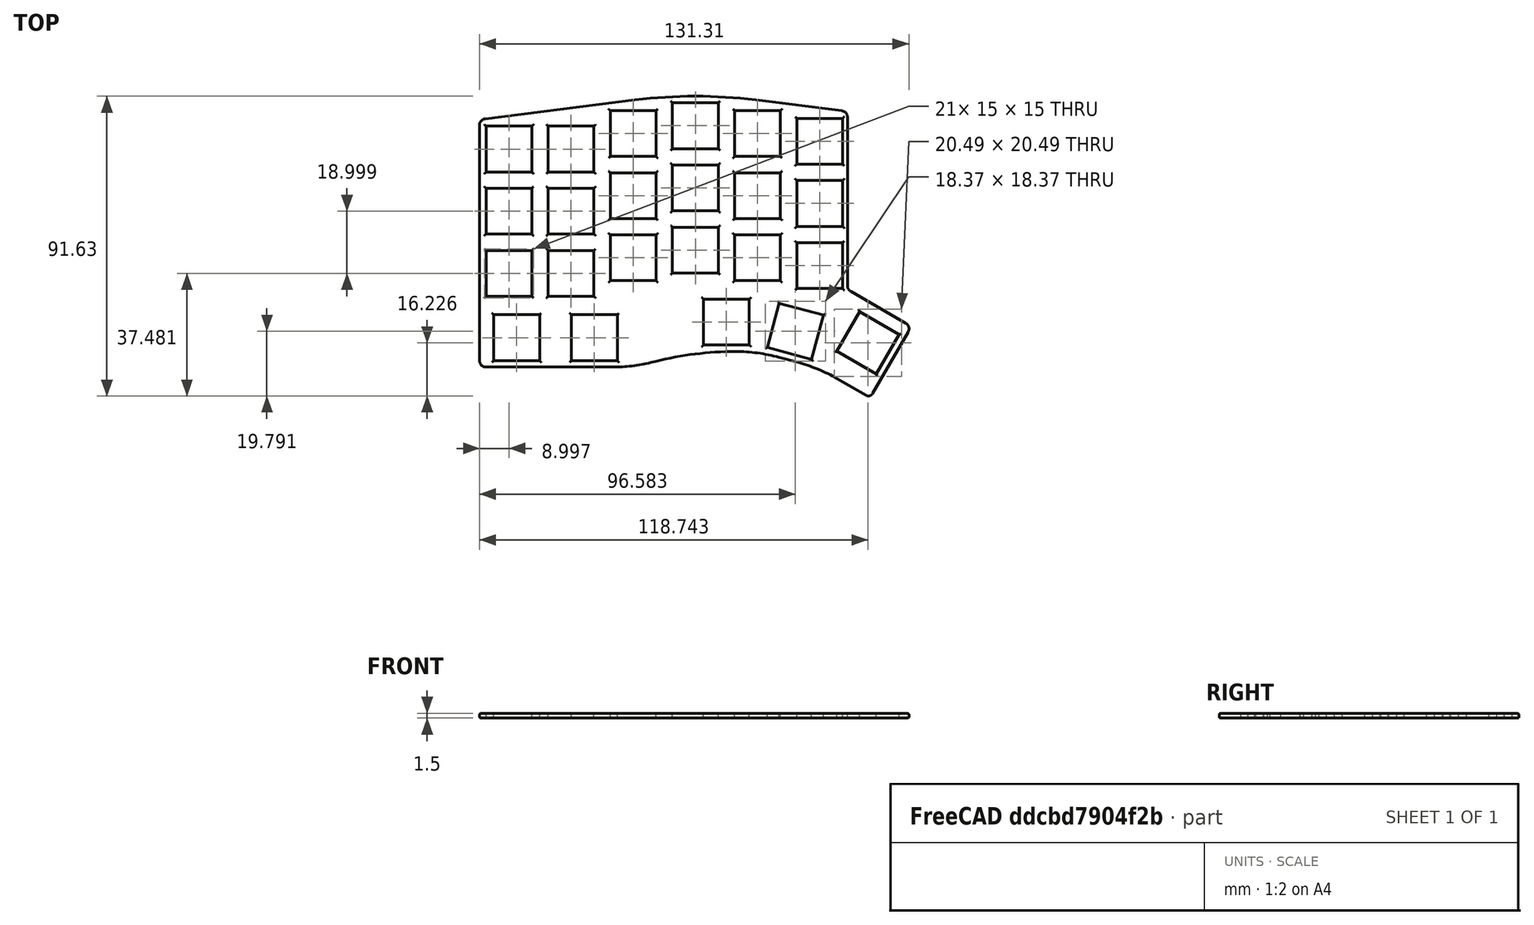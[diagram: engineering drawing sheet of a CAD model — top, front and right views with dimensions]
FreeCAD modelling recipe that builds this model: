
FCSTD DOCUMENT  (FreeCAD 0.21R)
Label: plate
License: All rights reserved
LicenseURL: http://en.wikipedia.org/wiki/All_rights_reserved
objects: Sketcher::SketchObject×1, PartDesign::Pad×1, PartDesign::Fillet×1, PartDesign::Body×1
note: 6 computed .brp shape members not serialized (recipe doc carries the construction recipe); baked Part::Feature solids carry a one-line shape summary decoded from their .brp

FEATURE [Sketcher::SketchObject] Sketch
  FullyConstrained = false
  sketch-geometry (113):
    g0: LineSegment StartX=-4.87291 StartY=42.5634 StartZ=0 EndX=9.12709 EndY=42.5634 EndZ=0
    g1: LineSegment StartX=-4.87291 StartY=28.5634 StartZ=0 EndX=9.12709 EndY=28.5634 EndZ=0
    g2: LineSegment StartX=-4.87291 StartY=42.5634 StartZ=0 EndX=-4.87291 EndY=28.5634 EndZ=0
    g3: LineSegment StartX=9.12709 StartY=42.5634 StartZ=0 EndX=9.12709 EndY=28.5634 EndZ=0
    g4: LineSegment StartX=-23.8729 StartY=40.1885 StartZ=0 EndX=-9.87291 EndY=40.1885 EndZ=0
    g5: LineSegment StartX=-23.8729 StartY=26.1885 StartZ=0 EndX=-9.87291 EndY=26.1885 EndZ=0
    g6: LineSegment StartX=-23.8729 StartY=40.1885 StartZ=0 EndX=-23.8729 EndY=26.1885 EndZ=0
    g7: LineSegment StartX=-9.87291 StartY=40.1885 StartZ=0 EndX=-9.87291 EndY=26.1885 EndZ=0
    g8: LineSegment StartX=14.1271 StartY=40.1885 StartZ=0 EndX=28.1271 EndY=40.1885 EndZ=0
    g9: LineSegment StartX=14.1271 StartY=26.1885 StartZ=0 EndX=28.1271 EndY=26.1885 EndZ=0
    g10: LineSegment StartX=14.1271 StartY=40.1885 StartZ=0 EndX=14.1271 EndY=26.1885 EndZ=0
    g11: LineSegment StartX=28.1271 StartY=40.1885 StartZ=0 EndX=28.1271 EndY=26.1885 EndZ=0
    g12: LineSegment StartX=33.1271 StartY=37.8136 StartZ=0 EndX=47.1271 EndY=37.8136 EndZ=0
    g13: LineSegment StartX=33.1271 StartY=23.8136 StartZ=0 EndX=47.1271 EndY=23.8136 EndZ=0
    g14: LineSegment StartX=33.1271 StartY=37.8136 StartZ=0 EndX=33.1271 EndY=23.8136 EndZ=0
    g15: LineSegment StartX=47.1271 StartY=37.8136 StartZ=0 EndX=47.1271 EndY=23.8136 EndZ=0
    g16: LineSegment StartX=-61.8729 StartY=35.4388 StartZ=0 EndX=-47.8729 EndY=35.4388 EndZ=0
    g17: LineSegment StartX=-61.8729 StartY=21.4388 StartZ=0 EndX=-47.8729 EndY=21.4388 EndZ=0
    g18: LineSegment StartX=-61.8729 StartY=35.4388 StartZ=0 EndX=-61.8729 EndY=21.4388 EndZ=0
    g19: LineSegment StartX=-47.8729 StartY=35.4388 StartZ=0 EndX=-47.8729 EndY=21.4388 EndZ=0
    g20: LineSegment StartX=-42.8729 StartY=35.4388 StartZ=0 EndX=-28.8729 EndY=35.4388 EndZ=0
    g21: LineSegment StartX=-42.8729 StartY=21.4388 StartZ=0 EndX=-28.8729 EndY=21.4388 EndZ=0
    g22: LineSegment StartX=-42.8729 StartY=35.4388 StartZ=0 EndX=-42.8729 EndY=21.4388 EndZ=0
    g23: LineSegment StartX=-28.8729 StartY=35.4388 StartZ=0 EndX=-28.8729 EndY=21.4388 EndZ=0
    g24: LineSegment StartX=-4.87291 StartY=23.5644 StartZ=0 EndX=9.12709 EndY=23.5644 EndZ=0
    g25: LineSegment StartX=-4.87291 StartY=9.56439 StartZ=0 EndX=9.12709 EndY=9.56439 EndZ=0
    g26: LineSegment StartX=-4.87291 StartY=23.5644 StartZ=0 EndX=-4.87291 EndY=9.56439 EndZ=0
    g27: LineSegment StartX=9.12709 StartY=23.5644 StartZ=0 EndX=9.12709 EndY=9.56439 EndZ=0
    g28: LineSegment StartX=-23.8729 StartY=21.1895 StartZ=0 EndX=-9.87291 EndY=21.1895 EndZ=0
    g29: LineSegment StartX=-23.8729 StartY=7.18952 StartZ=0 EndX=-9.87291 EndY=7.18952 EndZ=0
    g30: LineSegment StartX=-23.8729 StartY=21.1895 StartZ=0 EndX=-23.8729 EndY=7.18952 EndZ=0
    g31: LineSegment StartX=-9.87291 StartY=21.1895 StartZ=0 EndX=-9.87291 EndY=7.18952 EndZ=0
    g32: LineSegment StartX=14.1271 StartY=21.1895 StartZ=0 EndX=28.1271 EndY=21.1895 EndZ=0
    g33: LineSegment StartX=14.1271 StartY=7.18952 StartZ=0 EndX=28.1271 EndY=7.18952 EndZ=0
    g34: LineSegment StartX=14.1271 StartY=21.1895 StartZ=0 EndX=14.1271 EndY=7.18952 EndZ=0
    g35: LineSegment StartX=28.1271 StartY=21.1895 StartZ=0 EndX=28.1271 EndY=7.18952 EndZ=0
    g36: LineSegment StartX=33.1271 StartY=18.8146 StartZ=0 EndX=47.1271 EndY=18.8146 EndZ=0
    g37: LineSegment StartX=33.1271 StartY=4.81464 StartZ=0 EndX=47.1271 EndY=4.81464 EndZ=0
    g38: LineSegment StartX=33.1271 StartY=18.8146 StartZ=0 EndX=33.1271 EndY=4.81464 EndZ=0
    g39: LineSegment StartX=47.1271 StartY=18.8146 StartZ=0 EndX=47.1271 EndY=4.81464 EndZ=0
    g40: LineSegment StartX=-61.8729 StartY=16.4398 StartZ=0 EndX=-47.8729 EndY=16.4398 EndZ=0
    g41: LineSegment StartX=-61.8729 StartY=2.43977 StartZ=0 EndX=-47.8729 EndY=2.43977 EndZ=0
    g42: LineSegment StartX=-61.8729 StartY=16.4398 StartZ=0 EndX=-61.8729 EndY=2.43977 EndZ=0
    g43: LineSegment StartX=-47.8729 StartY=16.4398 StartZ=0 EndX=-47.8729 EndY=2.43977 EndZ=0
    g44: LineSegment StartX=-42.8729 StartY=16.4398 StartZ=0 EndX=-28.8729 EndY=16.4398 EndZ=0
    g45: LineSegment StartX=-42.8729 StartY=2.43977 StartZ=0 EndX=-28.8729 EndY=2.43977 EndZ=0
    g46: LineSegment StartX=-42.8729 StartY=16.4398 StartZ=0 EndX=-42.8729 EndY=2.43977 EndZ=0
    g47: LineSegment StartX=-28.8729 StartY=16.4398 StartZ=0 EndX=-28.8729 EndY=2.43977 EndZ=0
    g48: LineSegment StartX=-4.87291 StartY=4.56539 StartZ=0 EndX=9.12709 EndY=4.56539 EndZ=0
    g49: LineSegment StartX=-4.87291 StartY=-9.43461 StartZ=0 EndX=9.12709 EndY=-9.43461 EndZ=0
    g50: LineSegment StartX=-4.87291 StartY=4.56539 StartZ=0 EndX=-4.87291 EndY=-9.43461 EndZ=0
    g51: LineSegment StartX=9.12709 StartY=4.56539 StartZ=0 EndX=9.12709 EndY=-9.43461 EndZ=0
    g52: LineSegment StartX=14.1271 StartY=2.19052 StartZ=0 EndX=28.1271 EndY=2.19052 EndZ=0
    g53: LineSegment StartX=14.1271 StartY=-11.8095 StartZ=0 EndX=28.1271 EndY=-11.8095 EndZ=0
    g54: LineSegment StartX=14.1271 StartY=2.19052 StartZ=0 EndX=14.1271 EndY=-11.8095 EndZ=0
    g55: LineSegment StartX=28.1271 StartY=2.19052 StartZ=0 EndX=28.1271 EndY=-11.8095 EndZ=0
    g56: LineSegment StartX=-23.8729 StartY=2.18862 StartZ=0 EndX=-9.87291 EndY=2.18862 EndZ=0
    g57: LineSegment StartX=-23.8729 StartY=-11.8114 StartZ=0 EndX=-9.87291 EndY=-11.8114 EndZ=0
    g58: LineSegment StartX=-23.8729 StartY=2.18862 StartZ=0 EndX=-23.8729 EndY=-11.8114 EndZ=0
    g59: LineSegment StartX=-9.87291 StartY=2.18862 StartZ=0 EndX=-9.87291 EndY=-11.8114 EndZ=0
    g60: LineSegment StartX=33.1271 StartY=-0.18436 StartZ=0 EndX=47.1271 EndY=-0.18436 EndZ=0
    g61: LineSegment StartX=33.1271 StartY=-14.1844 StartZ=0 EndX=47.1271 EndY=-14.1844 EndZ=0
    g62: LineSegment StartX=33.1271 StartY=-0.18436 StartZ=0 EndX=33.1271 EndY=-14.1844 EndZ=0
    g63: LineSegment StartX=47.1271 StartY=-0.18436 StartZ=0 EndX=47.1271 EndY=-14.1844 EndZ=0
    g64: LineSegment StartX=-61.8729 StartY=-2.55923 StartZ=0 EndX=-47.8729 EndY=-2.55923 EndZ=0
    g65: LineSegment StartX=-61.8729 StartY=-16.5592 StartZ=0 EndX=-47.8729 EndY=-16.5592 EndZ=0
    g66: LineSegment StartX=-61.8729 StartY=-2.55923 StartZ=0 EndX=-61.8729 EndY=-16.5592 EndZ=0
    g67: LineSegment StartX=-47.8729 StartY=-2.55923 StartZ=0 EndX=-47.8729 EndY=-16.5592 EndZ=0
    g68: LineSegment StartX=-42.8729 StartY=-2.55923 StartZ=0 EndX=-28.8729 EndY=-2.55923 EndZ=0
    g69: LineSegment StartX=-42.8729 StartY=-16.5592 StartZ=0 EndX=-28.8729 EndY=-16.5592 EndZ=0
    g70: LineSegment StartX=-42.8729 StartY=-2.55923 StartZ=0 EndX=-42.8729 EndY=-16.5592 EndZ=0
    g71: LineSegment StartX=-28.8729 StartY=-2.55923 StartZ=0 EndX=-28.8729 EndY=-16.5592 EndZ=0
    g72: LineSegment StartX=4.62709 StartY=-17.4734 StartZ=0 EndX=18.6271 EndY=-17.4734 EndZ=0
    g73: LineSegment StartX=4.62709 StartY=-31.4734 StartZ=0 EndX=18.6271 EndY=-31.4734 EndZ=0
    g74: LineSegment StartX=4.62709 StartY=-17.4734 StartZ=0 EndX=4.62709 EndY=-31.4734 EndZ=0
    g75: LineSegment StartX=18.6271 StartY=-17.4734 StartZ=0 EndX=18.6271 EndY=-31.4734 EndZ=0
    g76: LineSegment StartX=-59.4979 StartY=-22.2232 StartZ=0 EndX=-45.4979 EndY=-22.2232 EndZ=0
    g77: LineSegment StartX=-59.4979 StartY=-36.2232 StartZ=0 EndX=-45.4979 EndY=-36.2232 EndZ=0
    g78: LineSegment StartX=-59.4979 StartY=-22.2232 StartZ=0 EndX=-59.4979 EndY=-36.2232 EndZ=0
    g79: LineSegment StartX=-45.4979 StartY=-22.2232 StartZ=0 EndX=-45.4979 EndY=-36.2232 EndZ=0
    g80: LineSegment StartX=-35.7479 StartY=-22.2232 StartZ=0 EndX=-21.7479 EndY=-22.2232 EndZ=0
    g81: LineSegment StartX=-35.7479 StartY=-36.2232 StartZ=0 EndX=-21.7479 EndY=-36.2232 EndZ=0
    g82: LineSegment StartX=-35.7479 StartY=-22.2232 StartZ=0 EndX=-35.7479 EndY=-36.2232 EndZ=0
    g83: LineSegment StartX=-21.7479 StartY=-22.2232 StartZ=0 EndX=-21.7479 EndY=-36.2232 EndZ=0
    g84: LineSegment StartX=27.7632 StartY=-18.6761 StartZ=0 EndX=41.2862 EndY=-22.2996 EndZ=0
    g85: LineSegment StartX=24.1398 StartY=-32.1991 StartZ=0 EndX=37.6627 EndY=-35.8225 EndZ=0
    g86: LineSegment StartX=27.7632 StartY=-18.6761 StartZ=0 EndX=24.1398 EndY=-32.1991 EndZ=0
    g87: LineSegment StartX=41.2862 StartY=-22.2996 StartZ=0 EndX=37.6627 EndY=-35.8225 EndZ=0
    g88: LineSegment StartX=64.4351 StartY=-28.2515 StartZ=0 EndX=57.4351 EndY=-40.3758 EndZ=0
    g89: LineSegment StartX=52.3107 StartY=-21.2515 StartZ=0 EndX=45.3107 EndY=-33.3758 EndZ=0
    g90: LineSegment StartX=64.4351 StartY=-28.2515 StartZ=0 EndX=52.3107 EndY=-21.2515 EndZ=0
    g91: LineSegment StartX=57.4351 StartY=-40.3758 StartZ=0 EndX=45.3107 EndY=-33.3758 EndZ=0
    g92: ArcOfCircle CenterX=50.6271 CenterY=-13.3512 CenterZ=0 NormalX=0 NormalY=0 NormalZ=1 AngleXU=0 Radius=2 StartAngle=3.14159 EndAngle=4.18879
    g93: ArcOfCircle CenterX=2.12709 CenterY=-103.909 CenterZ=0 NormalX=0 NormalY=0 NormalZ=1 AngleXU=0 Radius=148.5 StartAngle=1.44645 EndAngle=1.69514
    g94: ArcOfCircle CenterX=14.3883 CenterY=-84.9734 CenterZ=0 NormalX=0 NormalY=0 NormalZ=1 AngleXU=0 Radius=51.5 StartAngle=1.309 EndAngle=1.5708
    g95: LineSegment StartX=27.7175 StartY=-35.2283 StartZ=0 EndX=33.2016 EndY=-36.6977 EndZ=0
    g96: ArcOfCircle CenterX=19.8724 CenterY=-86.4429 CenterZ=0 NormalX=0 NormalY=0 NormalZ=1 AngleXU=0 Radius=51.5 StartAngle=1.0472 EndAngle=1.309
    g97: LineSegment StartX=54.2798 StartY=-46.8409 StartZ=0 EndX=45.6224 EndY=-41.8426 EndZ=0
    g98: ArcOfCircle CenterX=55.0298 CenterY=-45.5419 CenterZ=0 NormalX=0 NormalY=0 NormalZ=1 AngleXU=0 Radius=1.5 StartAngle=4.18879 EndAngle=5.75959
    g99: ArcOfCircle CenterX=-23.1357 CenterY=10.2768 CenterZ=0 NormalX=0 NormalY=0 NormalZ=1 AngleXU=0 Radius=48.5 StartAngle=4.71239 EndAngle=4.95543
    g100: LineSegment StartX=-11.4639 StartY=-36.7978 StartZ=0 EndX=-10.0872 EndY=-36.4565 EndZ=0
    g101: LineSegment StartX=-62.121 StartY=37.7164 StartZ=0 EndX=-16.2911 EndY=43.4448 EndZ=0
    g102: ArcOfCircle CenterX=-61.8729 CenterY=35.7318 CenterZ=0 NormalX=0 NormalY=0 NormalZ=1 AngleXU=0 Radius=2 StartAngle=1.69514 EndAngle=3.14159
    g103: LineSegment StartX=-23.1357 StartY=-38.2232 StartZ=0 EndX=-61.8729 EndY=-38.2232 EndZ=0
    g104: LineSegment StartX=-63.8729 StartY=-36.2232 StartZ=0 EndX=-63.8729 EndY=35.7318 EndZ=0
    g105: ArcOfCircle CenterX=-61.8729 CenterY=-36.2232 CenterZ=0 NormalX=0 NormalY=0 NormalZ=1 AngleXU=0 Radius=2 StartAngle=3.14159 EndAngle=4.71239
    g106: LineSegment StartX=67.1671 StartY=-27.5194 StartZ=0 EndX=56.3288 EndY=-46.2919 EndZ=0
    g107: LineSegment StartX=66.4351 StartY=-24.7874 StartZ=0 EndX=49.6271 EndY=-15.0833 EndZ=0
    g108: ArcOfCircle CenterX=65.4351 CenterY=-26.5194 CenterZ=0 NormalX=0 NormalY=0 NormalZ=1 AngleXU=0 Radius=2 StartAngle=5.75959 EndAngle=7.33038
    g109: ArcOfCircle CenterX=14.3638 CenterY=-135.174 CenterZ=0 NormalX=0 NormalY=0 NormalZ=1 AngleXU=0 Radius=101.701 StartAngle=1.57056 EndAngle=1.8136
    g110: LineSegment StartX=20.5453 StartY=43.4448 StartZ=0 EndX=46.8751 EndY=40.1537 EndZ=0
    g111: LineSegment StartX=48.6271 StartY=38.1692 StartZ=0 EndX=48.6271 EndY=-13.3512 EndZ=0
    g112: ArcOfCircle CenterX=46.6271 CenterY=38.1692 CenterZ=0 NormalX=0 NormalY=0 NormalZ=1 AngleXU=0 Radius=2 StartAngle=0 EndAngle=1.44645
  constraints (113):
    c: Coincident(g104,g105)
    c: Coincident(g102,g104)
    c: Coincident(g101,g102)
    c: Coincident(g103,g105)
    c: Coincident(g65,g66)
    c: Coincident(g64,g66)
    c: Coincident(g41,g42)
    c: Coincident(g40,g42)
    c: Coincident(g17,g18)
    c: Coincident(g16,g18)
    c: Coincident(g77,g78)
    c: Coincident(g76,g78)
    c: Coincident(g65,g67)
    c: Coincident(g64,g67)
    c: Coincident(g41,g43)
    c: Coincident(g40,g43)
    c: Coincident(g17,g19)
    c: Coincident(g16,g19)
    c: Coincident(g77,g79)
    c: Coincident(g76,g79)
    c: Coincident(g69,g70)
    c: Coincident(g68,g70)
    c: Coincident(g45,g46)
    c: Coincident(g44,g46)
    c: Coincident(g21,g22)
    c: Coincident(g20,g22)
    c: Coincident(g81,g82)
    c: Coincident(g80,g82)
    c: Coincident(g69,g71)
    c: Coincident(g68,g71)
    c: Coincident(g45,g47)
    c: Coincident(g44,g47)
    c: Coincident(g21,g23)
    c: Coincident(g20,g23)
    c: Coincident(g57,g58)
    c: Coincident(g56,g58)
    c: Coincident(g29,g30)
    c: Coincident(g28,g30)
    c: Coincident(g5,g6)
    c: Coincident(g4,g6)
    c: Coincident(g99,g103)
    c: Coincident(g81,g83)
    c: Coincident(g80,g83)
    c: Coincident(g93,g101)
    c: Coincident(g99,g100)
    c: Coincident(g100,g109)
    c: Coincident(g57,g59)
    c: Coincident(g56,g59)
    c: Coincident(g29,g31)
    c: Coincident(g28,g31)
    c: Coincident(g5,g7)
    c: Coincident(g4,g7)
    c: Coincident(g49,g50)
    c: Coincident(g48,g50)
    c: Coincident(g25,g26)
    c: Coincident(g24,g26)
    c: Coincident(g1,g2)
    c: Coincident(g0,g2)
    c: Coincident(g73,g74)
    c: Coincident(g72,g74)
    c: Coincident(g49,g51)
    c: Coincident(g48,g51)
    c: Coincident(g25,g27)
    c: Coincident(g24,g27)
    c: Coincident(g1,g3)
    c: Coincident(g0,g3)
    c: Coincident(g53,g54)
    c: Coincident(g52,g54)
    c: Coincident(g33,g34)
    c: Coincident(g32,g34)
    c: Coincident(g9,g10)
    c: Coincident(g8,g10)
    c: Coincident(g94,g109)
    c: Coincident(g73,g75)
    c: Coincident(g72,g75)
    c: Coincident(g93,g110)
    c: Coincident(g85,g86)
    c: Coincident(g94,g95)
    c: Coincident(g84,g86)
    c: Coincident(g53,g55)
    c: Coincident(g52,g55)
    c: Coincident(g33,g35)
    c: Coincident(g32,g35)
    c: Coincident(g9,g11)
    c: Coincident(g8,g11)
    c: Coincident(g61,g62)
    c: Coincident(g60,g62)
    c: Coincident(g37,g38)
    c: Coincident(g36,g38)
    c: Coincident(g13,g14)
    c: Coincident(g12,g14)
    c: Coincident(g95,g96)
    c: Coincident(g85,g87)
    c: Coincident(g84,g87)
    c: Coincident(g89,g91)
    c: Coincident(g96,g97)
    c: Coincident(g110,g112)
    c: Coincident(g61,g63)
    c: Coincident(g60,g63)
    c: Coincident(g37,g39)
    c: Coincident(g36,g39)
    c: Coincident(g13,g15)
    c: Coincident(g12,g15)
    c: Coincident(g92,g111)
    c: Coincident(g111,g112)
    c: Coincident(g92,g107)
    c: Coincident(g89,g90)
    c: Coincident(g97,g98)
    c: Coincident(g98,g106)
    c: Coincident(g88,g91)
    c: Coincident(g88,g90)
    c: Coincident(g107,g108)
    c: Coincident(g106,g108)
FEATURE [PartDesign::Pad] Pad
  Direction = (0,0,1)
  Length = 1.5
  Length2 = 10
  Profile = -> Sketch
  ReferenceAxis = -> Sketch [N_Axis]
  Type = 0
FEATURE [PartDesign::Fillet] Fillet
  Base = -> Pad [Face115,Face114]
  BaseFeature = -> Pad
  Radius = 0.5
  SupportTransform = false
  UseAllEdges = false
FEATURE [PartDesign::Body] Body  label="Corps"
  Group = -> [Sketch,Pad,Fillet]
  Origin = -> Origin
  Tip = -> Fillet
